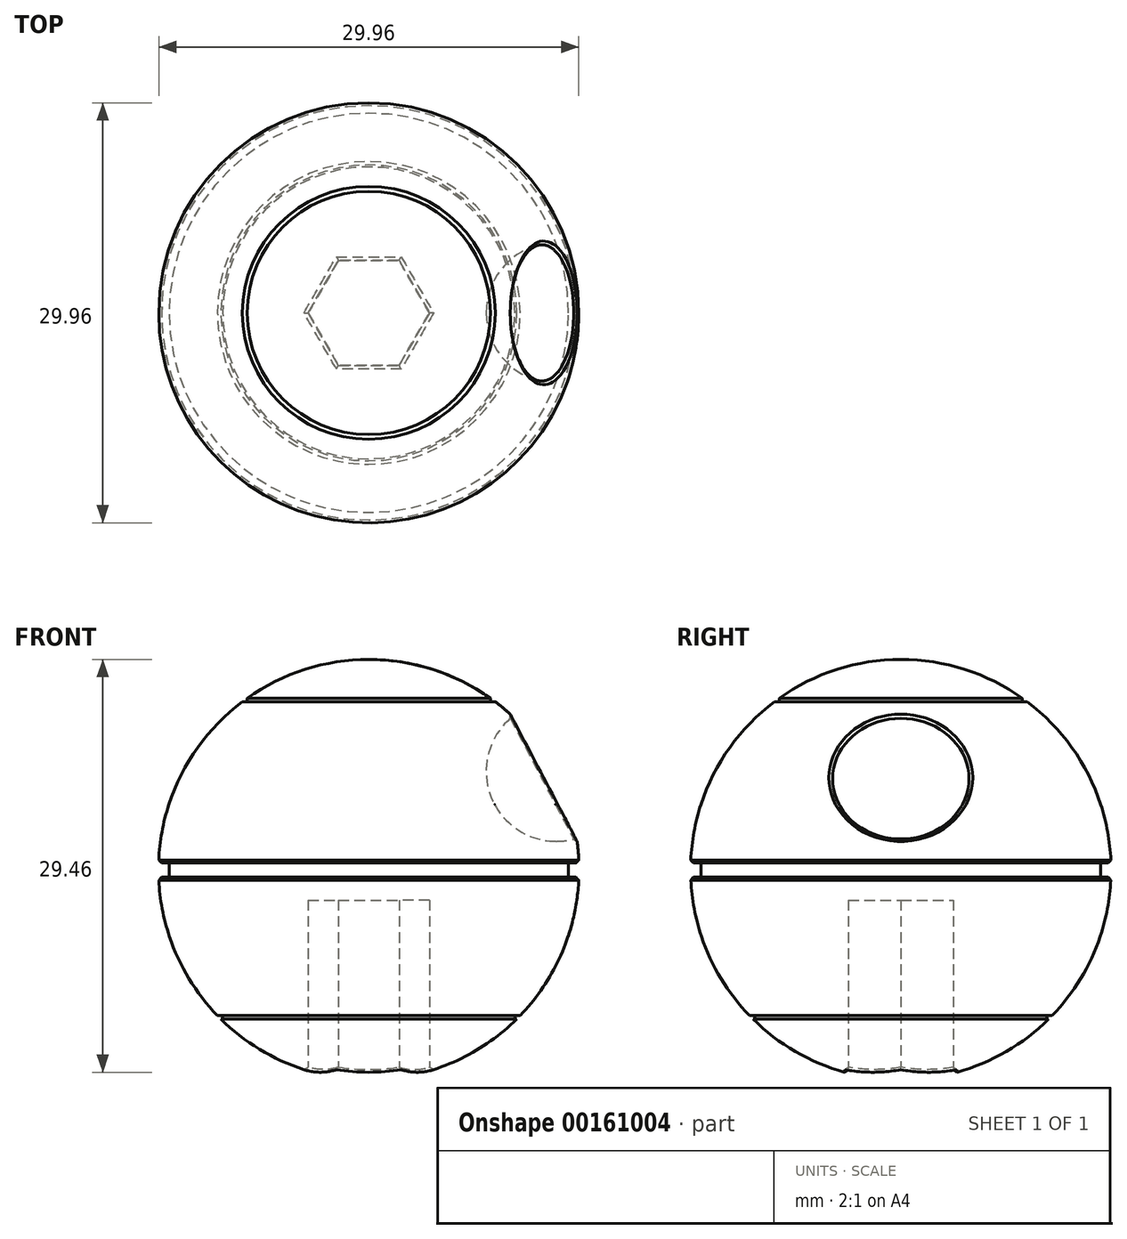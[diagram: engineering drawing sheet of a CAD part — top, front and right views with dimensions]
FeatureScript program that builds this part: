
annotation { "Feature Type Name" : "Feature", "Feature Type Description" : "" }
export const myFeature = defineFeature(function(context is Context, id is Id, definition is map)
    precondition{}
    {
        {
            var Q0;
            Q0=qCreatedBy(makeId("Front.planeOp"),FACE);
            var sketch = newSketch(context, id + "F0", { "sketchPlane" : qUnion([Q0])});
            skLineSegment(sketch, "E0", {"start": v(0, 15.2) * mm, "end": v(0, -14.8) * mm, "construction": true});
            skArc(sketch, "E1", {"start": v(0, -14.8) * mm, "mid": v(5.7, -13.68) * mm, "end": v(10.55, -10.47) * mm});
            skLineSegment(sketch, "E2.bottom", {"start": v(14.24, 0.67) * mm, "end": v(15, 0.67) * mm});
            skLineSegment(sketch, "E2.top", {"start": v(14.24, -0.34) * mm, "end": v(15, -0.34) * mm});
            skLineSegment(sketch, "E2.left", {"start": v(14.24, 0.67) * mm, "end": v(14.24, -0.34) * mm});
            skArc(sketch, "E3.trimOffspring", {"start": v(15, 0.67) * mm, "mid": v(14.77, 2.78) * mm, "end": v(14.26, 4.84) * mm});
            skLineSegment(sketch, "E4", {"start": v(0, 15.2) * mm, "end": v(0, -14.8) * mm});
            skLineSegment(sketch, "E5", {"start": v(8.68, 12.43) * mm, "end": v(8.68, 12.18) * mm});
            skLineSegment(sketch, "E6", {"start": v(8.68, 12.18) * mm, "end": v(9.02, 12.18) * mm});
            skLineSegment(sketch, "E7", {"start": v(10.8, -10.22) * mm, "end": v(10.42, -10.22) * mm});
            skLineSegment(sketch, "E8", {"start": v(10.42, -10.22) * mm, "end": v(10.42, -10.47) * mm});
            skLineSegment(sketch, "E9", {"start": v(10.42, -10.47) * mm, "end": v(10.55, -10.47) * mm});
            skArc(sketch, "E10.trimOffspring", {"start": v(10.8, -10.22) * mm, "mid": v(12.83, -7.58) * mm, "end": v(14.23, -4.57) * mm});
            skArc(sketch, "E11.trimOffspring", {"start": v(14.22, -4.57) * mm, "mid": v(14.76, -2.49) * mm, "end": v(15, -0.34) * mm});
            skArc(sketch, "E12.trimOffspring", {"start": v(14.26, 4.84) * mm, "mid": v(12.2, 8.91) * mm, "end": v(9.02, 12.18) * mm});
            skArc(sketch, "E13.trimOffspring", {"start": v(8.68, 12.43) * mm, "mid": v(4.55, 14.48) * mm, "end": v(0, 15.2) * mm});
            skSolve(sketch);
        }
        {
            var Q0;
            Q0=makeQuery(id+"F0.imprint","IMPRINT",FACE,{"disambiguationData":[TD([[makeQuery(id+"F0.imprint","IMPRINT",EDGE,{"derivedFrom":sQuery(id+"F0.wireOp",EDGE,"E1")}),1.0]])]});
            var Q1;
            Q1=sQuery(id+"F0.wireOp",EDGE,"E4");
            revolve(context, id + "F1", {"entities" : qUnion([Q0]), "axis" : qUnion([Q1]), "revolveType" : RevolveType.FULL});
        }
        {
            var Q0;
            Q0=qCreatedBy(makeId("Front.planeOp"),FACE);
            var sketch = newSketch(context, id + "F2", { "sketchPlane" : qUnion([Q0])});
            skLineSegment(sketch, "E14", {"start": v(0, 4.64) * mm, "end": v(0, 14.64) * mm});
            skArc(sketch, "E15", {"start": v(0, 4.64) * mm, "mid": v(5, 9.64) * mm, "end": v(0, 14.64) * mm});
            skSolve(sketch);
        }
        {
            var Q0;
            Q0=makeQuery(id+"F2.imprint","IMPRINT",FACE,{"disambiguationData":[TD([[makeQuery(id+"F2.imprint","IMPRINT",EDGE,{"derivedFrom":sQuery(id+"F2.wireOp",EDGE,"E14")}),-1.0]])]});
            var Q1;
            Q1=sQuery(id+"F2.wireOp",EDGE,"E14");
            revolve(context, id + "F3", {"entities" : qUnion([Q0]), "axis" : qUnion([Q1]), "revolveType" : RevolveType.FULL});
        }
        {
            var Q0;
            Q0=makeQuery(id+"F3.opRevolve","SWEPT_BODY",BODY,{"disambiguationData":[OSD([sQuery(id+"F2.wireOp",EDGE,"E14"),sQuery(id+"F2.wireOp",EDGE,"E15")])]});
            transform(context, id + "F4", {"entities" : qUnion([Q0]), "transformType" : TransformType.TRANSLATION_3D, "dx" : 13.38 * mm, "dy" : 0 * mm, "dz" : -2.42 * mm, "makeCopy" : false});
        }
        {
            var Q0;
            Q0=makeQuery(id+"F3.opRevolve","SWEPT_BODY",BODY,{"disambiguationData":[OSD([sQuery(id+"F2.wireOp",EDGE,"E14"),sQuery(id+"F2.wireOp",EDGE,"E15")])]});
            var Q1;
            Q1=makeQuery(id+"F1.opRevolve","SWEPT_BODY",BODY,{"disambiguationData":[OSD([sQuery(id+"F0.wireOp",EDGE,"E1"),sQuery(id+"F0.wireOp",EDGE,"E2.bottom"),sQuery(id+"F0.wireOp",EDGE,"E2.top"),sQuery(id+"F0.wireOp",EDGE,"E2.left"),sQuery(id+"F0.wireOp",EDGE,"E3.trimOffspring"),sQuery(id+"F0.wireOp",EDGE,"E4")])]});
            booleanBodies(context, id + "F5", {"operationType" : BooleanOperationType.SUBTRACTION, "tools" : qUnion([Q0]), "targets" : qUnion([Q1])});
        }
        {
            var Q0;
            Q0=qCreatedBy(makeId("Top.planeOp"),FACE);
            var sketch = newSketch(context, id + "F6", { "sketchPlane" : qUnion([Q0])});
            skCircle(sketch, "E16.cCircle", {"center": v(0, 0) * mm, "radius": 3.75 * mm, "construction": true});
            skLineSegment(sketch, "E16.0", {"start": v(-2.17, 3.75) * mm, "end": v(2.17, 3.75) * mm});
            skLineSegment(sketch, "E16.1", {"start": v(2.17, 3.75) * mm, "end": v(4.33, 0) * mm});
            skLineSegment(sketch, "E16.2", {"start": v(4.33, 0) * mm, "end": v(2.17, -3.75) * mm});
            skLineSegment(sketch, "E16.3", {"start": v(2.17, -3.75) * mm, "end": v(-2.17, -3.75) * mm});
            skLineSegment(sketch, "E16.4", {"start": v(-2.17, -3.75) * mm, "end": v(-4.33, 0) * mm});
            skLineSegment(sketch, "E16.5", {"start": v(-4.33, 0) * mm, "end": v(-2.17, 3.75) * mm});
            skPoint(sketch, "E16.0.midPoint", {"position": v(0, 3.75) * mm});
            skSolve(sketch);
        }
        {
            var Q0;
            Q0=makeQuery(id+"F1.opRevolve","SWEPT_BODY",BODY,{"disambiguationData":[OSD([sQuery(id+"F0.wireOp",EDGE,"E1"),sQuery(id+"F0.wireOp",EDGE,"E2.bottom"),sQuery(id+"F0.wireOp",EDGE,"E2.top"),sQuery(id+"F0.wireOp",EDGE,"E2.left"),sQuery(id+"F0.wireOp",EDGE,"E3.trimOffspring"),sQuery(id+"F0.wireOp",EDGE,"E4")])]});
            transform(context, id + "F7", {"entities" : qUnion([Q0]), "transformType" : TransformType.TRANSLATION_3D, "dx" : 0 * mm, "dy" : 0 * mm, "dz" : 14.97 * mm, "makeCopy" : false});
        }
        {
            var Q0;
            Q0=makeQuery(id+"F6.imprint","IMPRINT",FACE,{"disambiguationData":[TD([[makeQuery(id+"F6.imprint","IMPRINT",EDGE,{"derivedFrom":sQuery(id+"F6.wireOp",EDGE,"E16.0")}),-1.0]])]});
            extrude(context, id + "F8", {"entities" : qUnion([Q0]), "operationType" : NewBodyOperationType.REMOVE, "depth" : 13 * mm});
        }
        {
            var Q0;
            Q0=makeQuery(id+"F1.opRevolve","SWEPT_EDGE",EDGE,{"disambiguationData":[OSD([sQuery(id+"F0.wireOp",EDGE,"E2.bottom"),sQuery(id+"F0.wireOp",EDGE,"E3.trimOffspring")])]});
            var Q1;
            Q1=makeQuery(id+"F1.opRevolve","SWEPT_EDGE",EDGE,{"disambiguationData":[OSD([sQuery(id+"F0.wireOp",EDGE,"E2.top"),sQuery(id+"F0.wireOp",EDGE,"E11.trimOffspring")])]});
            var Q2;
            Q2=makeQuery(id+"F8.boolean.opBoolean","INTERSECT",EDGE,{"derivedFrom":[makeQuery(id+"F1.opRevolve","SWEPT_FACE",FACE,{"disambiguationData":[OSD([sQuery(id+"F0.wireOp",EDGE,"E1")])]}),makeQuery(id+"F8.opExtrude","SWEPT_FACE",FACE,{"disambiguationData":[OSD([sQuery(id+"F6.wireOp",EDGE,"E16.2")])]})]});
            var Q3;
            Q3=makeQuery(id+"F8.boolean.opBoolean","INTERSECT",EDGE,{"derivedFrom":[makeQuery(id+"F1.opRevolve","SWEPT_FACE",FACE,{"disambiguationData":[OSD([sQuery(id+"F0.wireOp",EDGE,"E1")])]}),makeQuery(id+"F8.opExtrude","SWEPT_FACE",FACE,{"disambiguationData":[OSD([sQuery(id+"F6.wireOp",EDGE,"E16.3")])]})]});
            var Q4;
            Q4=makeQuery(id+"F8.boolean.opBoolean","INTERSECT",EDGE,{"derivedFrom":[makeQuery(id+"F1.opRevolve","SWEPT_FACE",FACE,{"disambiguationData":[OSD([sQuery(id+"F0.wireOp",EDGE,"E1")])]}),makeQuery(id+"F8.opExtrude","SWEPT_FACE",FACE,{"disambiguationData":[OSD([sQuery(id+"F6.wireOp",EDGE,"E16.4")])]})]});
            var Q5;
            Q5=makeQuery(id+"F8.boolean.opBoolean","INTERSECT",EDGE,{"derivedFrom":[makeQuery(id+"F1.opRevolve","SWEPT_FACE",FACE,{"disambiguationData":[OSD([sQuery(id+"F0.wireOp",EDGE,"E1")])]}),makeQuery(id+"F8.opExtrude","SWEPT_FACE",FACE,{"disambiguationData":[OSD([sQuery(id+"F6.wireOp",EDGE,"E16.5")])]})]});
            var Q6;
            Q6=makeQuery(id+"F8.boolean.opBoolean","INTERSECT",EDGE,{"derivedFrom":[makeQuery(id+"F1.opRevolve","SWEPT_FACE",FACE,{"disambiguationData":[OSD([sQuery(id+"F0.wireOp",EDGE,"E1")])]}),makeQuery(id+"F8.opExtrude","SWEPT_FACE",FACE,{"disambiguationData":[OSD([sQuery(id+"F6.wireOp",EDGE,"E16.1")])]})]});
            var Q7;
            Q7=makeQuery(id+"F8.boolean.opBoolean","INTERSECT",EDGE,{"derivedFrom":[makeQuery(id+"F1.opRevolve","SWEPT_FACE",FACE,{"disambiguationData":[OSD([sQuery(id+"F0.wireOp",EDGE,"E1")])]}),makeQuery(id+"F8.opExtrude","SWEPT_FACE",FACE,{"disambiguationData":[OSD([sQuery(id+"F6.wireOp",EDGE,"E16.0")])]})]});
            var Q8;
            Q8=makeQuery(id+"F5.opBoolean","INTERSECT",EDGE,{"derivedFrom":[makeQuery(id+"F1.opRevolve","SWEPT_FACE",FACE,{"disambiguationData":[OSD([sQuery(id+"F0.wireOp",EDGE,"E3.trimOffspring"),sQuery(id+"F0.wireOp",EDGE,"E12.trimOffspring")])]}),makeQuery(id+"F3.opRevolve","SWEPT_FACE",FACE,{"disambiguationData":[OSD([sQuery(id+"F2.wireOp",EDGE,"E15")])]})]});
            chamfer(context, id + "F9", {"entities" : qUnion([Q0, Q1, Q2, Q3, Q4, Q5, Q6, Q7, Q8]), "width" : .2 * mm, "tangentPropagation" : true});
        }
    });
